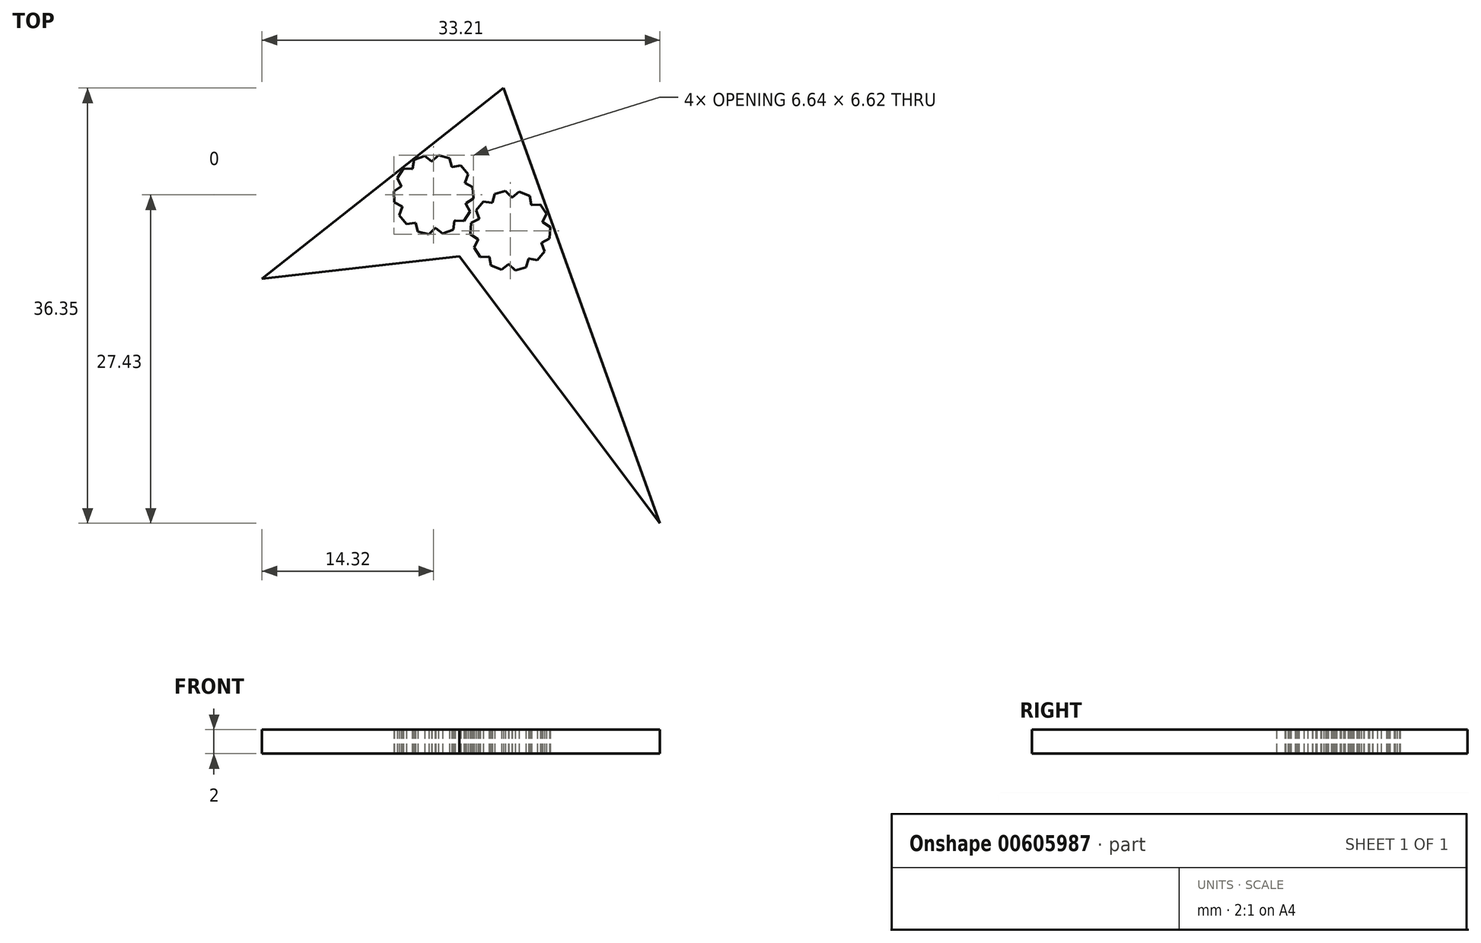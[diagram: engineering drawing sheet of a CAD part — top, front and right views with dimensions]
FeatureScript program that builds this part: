
annotation { "Feature Type Name" : "Feature", "Feature Type Description" : "" }
export const myFeature = defineFeature(function(context is Context, id is Id, definition is map)
    precondition{}
    {
        {
            var Q0;
            Q0=qCreatedBy(makeId("Top.planeOp"),FACE);
            var sketch = newSketch(context, id + "F0", { "sketchPlane" : qUnion([Q0])});
            skLineSegment(sketch, "E0", {"start": v(18, -24) * mm, "end": v(4, 15) * mm});
            skLineSegment(sketch, "E1", {"start": v(4, 15) * mm, "end": v(-17.5, -2) * mm});
            skLineSegment(sketch, "E2", {"start": v(-17.5, -2) * mm, "end": v(0, 0) * mm});
            skLineSegment(sketch, "E3", {"start": v(0, 0) * mm, "end": v(18, -24) * mm});
            skArc(sketch, "E4", {"start": v(-4.38, 6.27) * mm, "mid": v(-4.41, 6.15) * mm, "end": v(-4.45, 6.02) * mm, "construction": true});
            skLineSegment(sketch, "E5", {"start": v(-2, 8) * mm, "end": v(-1.51, 8.48) * mm});
            skLineSegment(sketch, "E6", {"start": v(-1.51, 8.48) * mm, "end": v(-0.93, 8.32) * mm});
            skLineSegment(sketch, "E7", {"start": v(-0.93, 8.32) * mm, "end": v(-0.75, 7.67) * mm});
            skLineSegment(sketch, "E8", {"start": v(-2, 5.5) * mm, "end": v(-1.22, 8.4) * mm, "construction": true});
            skLineSegment(sketch, "E9", {"start": v(-2, 8) * mm, "end": v(-2, 5.5) * mm, "construction": true});
            skLineSegment(sketch, "E10", {"start": v(-2, 5.5) * mm, "end": v(-0.75, 7.67) * mm, "construction": true});
            skLineSegment(sketch, "E11.1.0", {"start": v(-3.47, 7.52) * mm, "end": v(-3.36, 8.2) * mm});
            skLineSegment(sketch, "E11.1.1", {"start": v(-3.36, 8.2) * mm, "end": v(-2.8, 8.4) * mm});
            skLineSegment(sketch, "E11.1.2", {"start": v(-2.8, 8.4) * mm, "end": v(-2.26, 7.99) * mm});
            skLineSegment(sketch, "E11.2.0", {"start": v(-4.38, 6.27) * mm, "end": v(-4.68, 6.88) * mm});
            skLineSegment(sketch, "E11.2.1", {"start": v(-4.68, 6.88) * mm, "end": v(-4.35, 7.39) * mm});
            skLineSegment(sketch, "E11.2.2", {"start": v(-4.35, 7.39) * mm, "end": v(-3.67, 7.36) * mm});
            skLineSegment(sketch, "E11.3.0", {"start": v(-4.38, 4.73) * mm, "end": v(-4.98, 5.04) * mm});
            skLineSegment(sketch, "E11.3.1", {"start": v(-4.98, 5.04) * mm, "end": v(-5.01, 5.64) * mm});
            skLineSegment(sketch, "E11.3.2", {"start": v(-5.01, 5.64) * mm, "end": v(-4.45, 6.02) * mm});
            skLineSegment(sketch, "E11.4.0", {"start": v(-3.47, 3.48) * mm, "end": v(-4.14, 3.38) * mm});
            skLineSegment(sketch, "E11.4.1", {"start": v(-4.14, 3.38) * mm, "end": v(-4.52, 3.85) * mm});
            skLineSegment(sketch, "E11.4.2", {"start": v(-4.52, 3.85) * mm, "end": v(-4.28, 4.48) * mm});
            skLineSegment(sketch, "E11.5.0", {"start": v(-2, 3) * mm, "end": v(-2.49, 2.52) * mm});
            skLineSegment(sketch, "E11.5.1", {"start": v(-2.49, 2.52) * mm, "end": v(-3.07, 2.68) * mm});
            skLineSegment(sketch, "E11.5.2", {"start": v(-3.07, 2.68) * mm, "end": v(-3.25, 3.33) * mm});
            skLineSegment(sketch, "E11.6.0", {"start": v(-0.53, 3.48) * mm, "end": v(-0.64, 2.8) * mm});
            skLineSegment(sketch, "E11.6.1", {"start": v(-0.64, 2.8) * mm, "end": v(-1.2, 2.6) * mm});
            skLineSegment(sketch, "E11.6.2", {"start": v(-1.2, 2.6) * mm, "end": v(-1.74, 3.01) * mm});
            skLineSegment(sketch, "E11.7.0", {"start": v(0.38, 4.73) * mm, "end": v(0.68, 4.12) * mm});
            skLineSegment(sketch, "E11.7.1", {"start": v(0.68, 4.12) * mm, "end": v(0.35, 3.61) * mm});
            skLineSegment(sketch, "E11.7.2", {"start": v(0.35, 3.61) * mm, "end": v(-0.33, 3.64) * mm});
            skLineSegment(sketch, "E11.8.0", {"start": v(0.38, 6.27) * mm, "end": v(0.98, 5.96) * mm});
            skLineSegment(sketch, "E11.8.1", {"start": v(0.98, 5.96) * mm, "end": v(1.01, 5.36) * mm});
            skLineSegment(sketch, "E11.8.2", {"start": v(1.01, 5.36) * mm, "end": v(0.45, 4.98) * mm});
            skLineSegment(sketch, "E11.9.0", {"start": v(-0.53, 7.52) * mm, "end": v(0.14, 7.62) * mm});
            skLineSegment(sketch, "E11.9.1", {"start": v(0.14, 7.62) * mm, "end": v(0.52, 7.15) * mm});
            skLineSegment(sketch, "E11.9.2", {"start": v(0.52, 7.15) * mm, "end": v(0.28, 6.52) * mm});
            skArc(sketch, "E12", {"start": v(2.12, 3.52) * mm, "mid": v(2.07, 3.4) * mm, "end": v(2.02, 3.27) * mm, "construction": true});
            skLineSegment(sketch, "E13", {"start": v(3.15, 4.67) * mm, "end": v(3.33, 5.32) * mm});
            skLineSegment(sketch, "E14", {"start": v(3.33, 5.32) * mm, "end": v(3.91, 5.48) * mm});
            skLineSegment(sketch, "E15", {"start": v(3.91, 5.48) * mm, "end": v(4.4, 5) * mm});
            skLineSegment(sketch, "E16", {"start": v(4.4, 2.5) * mm, "end": v(3.62, 5.4) * mm, "construction": true});
            skLineSegment(sketch, "E17", {"start": v(3.15, 4.67) * mm, "end": v(4.4, 2.5) * mm, "construction": true});
            skLineSegment(sketch, "E18", {"start": v(4.4, 2.5) * mm, "end": v(4.4, 5) * mm, "construction": true});
            skLineSegment(sketch, "E19.1.0", {"start": v(2.12, 3.52) * mm, "end": v(1.88, 4.15) * mm});
            skLineSegment(sketch, "E19.1.1", {"start": v(1.88, 4.15) * mm, "end": v(2.26, 4.62) * mm});
            skLineSegment(sketch, "E19.1.2", {"start": v(2.26, 4.62) * mm, "end": v(2.93, 4.52) * mm});
            skLineSegment(sketch, "E19.2.0", {"start": v(1.95, 1.98) * mm, "end": v(1.39, 2.36) * mm});
            skLineSegment(sketch, "E19.2.1", {"start": v(1.39, 2.36) * mm, "end": v(1.42, 2.96) * mm});
            skLineSegment(sketch, "E19.2.2", {"start": v(1.42, 2.96) * mm, "end": v(2.02, 3.27) * mm});
            skLineSegment(sketch, "E19.3.0", {"start": v(2.73, 0.64) * mm, "end": v(2.05, 0.61) * mm});
            skLineSegment(sketch, "E19.3.1", {"start": v(2.05, 0.61) * mm, "end": v(1.72, 1.12) * mm});
            skLineSegment(sketch, "E19.3.2", {"start": v(1.72, 1.12) * mm, "end": v(2.02, 1.73) * mm});
            skLineSegment(sketch, "E19.4.0", {"start": v(4.14, 0.01) * mm, "end": v(3.6, -0.4) * mm});
            skLineSegment(sketch, "E19.4.1", {"start": v(3.6, -0.4) * mm, "end": v(3.04, -0.2) * mm});
            skLineSegment(sketch, "E19.4.2", {"start": v(3.04, -0.2) * mm, "end": v(2.93, 0.48) * mm});
            skLineSegment(sketch, "E19.5.0", {"start": v(5.65, 0.33) * mm, "end": v(5.47, -0.32) * mm});
            skLineSegment(sketch, "E19.5.1", {"start": v(5.47, -0.32) * mm, "end": v(4.89, -0.48) * mm});
            skLineSegment(sketch, "E19.5.2", {"start": v(4.89, -0.48) * mm, "end": v(4.4, 0) * mm});
            skLineSegment(sketch, "E19.6.0", {"start": v(6.68, 1.48) * mm, "end": v(6.92, 0.85) * mm});
            skLineSegment(sketch, "E19.6.1", {"start": v(6.92, 0.85) * mm, "end": v(6.54, 0.38) * mm});
            skLineSegment(sketch, "E19.6.2", {"start": v(6.54, 0.38) * mm, "end": v(5.87, 0.48) * mm});
            skLineSegment(sketch, "E19.7.0", {"start": v(6.85, 3.02) * mm, "end": v(7.41, 2.64) * mm});
            skLineSegment(sketch, "E19.7.1", {"start": v(7.41, 2.64) * mm, "end": v(7.38, 2.04) * mm});
            skLineSegment(sketch, "E19.7.2", {"start": v(7.38, 2.04) * mm, "end": v(6.78, 1.73) * mm});
            skLineSegment(sketch, "E19.8.0", {"start": v(6.07, 4.36) * mm, "end": v(6.75, 4.39) * mm});
            skLineSegment(sketch, "E19.8.1", {"start": v(6.75, 4.39) * mm, "end": v(7.08, 3.88) * mm});
            skLineSegment(sketch, "E19.8.2", {"start": v(7.08, 3.88) * mm, "end": v(6.78, 3.27) * mm});
            skLineSegment(sketch, "E19.9.0", {"start": v(4.66, 4.99) * mm, "end": v(5.2, 5.4) * mm});
            skLineSegment(sketch, "E19.9.1", {"start": v(5.2, 5.4) * mm, "end": v(5.76, 5.2) * mm});
            skLineSegment(sketch, "E19.9.2", {"start": v(5.76, 5.2) * mm, "end": v(5.87, 4.52) * mm});
            skArc(sketch, "E20", {"start": v(-4.38, 4.73) * mm, "mid": v(-4.33, 4.6) * mm, "end": v(-4.28, 4.48) * mm});
            skArc(sketch, "E21", {"start": v(2.12, 3.52) * mm, "mid": v(2.07, 3.4) * mm, "end": v(2.02, 3.27) * mm});
            skArc(sketch, "E22.trimOffspring", {"start": v(-4.38, 4.73) * mm, "mid": v(-4.33, 4.6) * mm, "end": v(-4.28, 4.48) * mm, "construction": true});
            skArc(sketch, "E23.trimOffspring", {"start": v(-3.47, 3.48) * mm, "mid": v(-3.36, 3.4) * mm, "end": v(-3.25, 3.33) * mm, "construction": true});
            skArc(sketch, "E24.trimOffspring", {"start": v(-4.38, 6.27) * mm, "mid": v(-4.41, 6.15) * mm, "end": v(-4.45, 6.02) * mm});
            skArc(sketch, "E25.trimOffspring", {"start": v(-3.47, 3.48) * mm, "mid": v(-3.36, 3.4) * mm, "end": v(-3.25, 3.33) * mm});
            skArc(sketch, "E26.trimOffspring", {"start": v(-2, 3) * mm, "mid": v(-1.87, 3) * mm, "end": v(-1.74, 3.01) * mm, "construction": true});
            skArc(sketch, "E27.trimOffspring", {"start": v(-2, 3) * mm, "mid": v(-1.87, 3) * mm, "end": v(-1.74, 3.01) * mm});
            skArc(sketch, "E28.trimOffspring", {"start": v(-0.53, 3.48) * mm, "mid": v(-0.43, 3.56) * mm, "end": v(-0.33, 3.64) * mm, "construction": true});
            skArc(sketch, "E29.trimOffspring", {"start": v(-0.53, 3.48) * mm, "mid": v(-0.43, 3.56) * mm, "end": v(-0.33, 3.64) * mm});
            skArc(sketch, "E30.trimOffspring", {"start": v(0.38, 4.73) * mm, "mid": v(0.41, 4.85) * mm, "end": v(0.45, 4.98) * mm, "construction": true});
            skArc(sketch, "E31.trimOffspring", {"start": v(0.38, 4.73) * mm, "mid": v(0.41, 4.85) * mm, "end": v(0.45, 4.98) * mm});
            skArc(sketch, "E32.trimOffspring", {"start": v(0.38, 6.27) * mm, "mid": v(0.33, 6.4) * mm, "end": v(0.28, 6.52) * mm, "construction": true});
            skArc(sketch, "E33.trimOffspring", {"start": v(0.38, 6.27) * mm, "mid": v(0.33, 6.4) * mm, "end": v(0.28, 6.52) * mm});
            skArc(sketch, "E34.trimOffspring", {"start": v(-0.53, 7.52) * mm, "mid": v(-0.64, 7.6) * mm, "end": v(-0.75, 7.67) * mm, "construction": true});
            skArc(sketch, "E35.trimOffspring", {"start": v(-0.53, 7.52) * mm, "mid": v(-0.64, 7.6) * mm, "end": v(-0.75, 7.67) * mm});
            skArc(sketch, "E36.trimOffspring", {"start": v(-3.47, 7.52) * mm, "mid": v(-3.57, 7.44) * mm, "end": v(-3.67, 7.36) * mm, "construction": true});
            skArc(sketch, "E37.trimOffspring", {"start": v(-3.47, 7.52) * mm, "mid": v(-3.57, 7.44) * mm, "end": v(-3.67, 7.36) * mm});
            skArc(sketch, "E38.trimOffspring", {"start": v(-2, 8) * mm, "mid": v(-2.13, 8) * mm, "end": v(-2.26, 7.99) * mm, "construction": true});
            skArc(sketch, "E39.trimOffspring", {"start": v(-2, 8) * mm, "mid": v(-2.13, 8) * mm, "end": v(-2.26, 7.99) * mm});
            skArc(sketch, "E40.trimOffspring", {"start": v(3.15, 4.67) * mm, "mid": v(3.04, 4.6) * mm, "end": v(2.93, 4.52) * mm, "construction": true});
            skArc(sketch, "E41.trimOffspring", {"start": v(3.15, 4.67) * mm, "mid": v(3.04, 4.6) * mm, "end": v(2.93, 4.52) * mm});
            skArc(sketch, "E42.trimOffspring", {"start": v(4.66, 4.99) * mm, "mid": v(4.53, 5) * mm, "end": v(4.4, 5) * mm, "construction": true});
            skArc(sketch, "E43.trimOffspring", {"start": v(4.66, 4.99) * mm, "mid": v(4.53, 5) * mm, "end": v(4.4, 5) * mm});
            skArc(sketch, "E44.trimOffspring", {"start": v(6.07, 4.36) * mm, "mid": v(5.97, 4.44) * mm, "end": v(5.87, 4.52) * mm, "construction": true});
            skArc(sketch, "E45.trimOffspring", {"start": v(6.07, 4.36) * mm, "mid": v(5.97, 4.44) * mm, "end": v(5.87, 4.52) * mm});
            skArc(sketch, "E46.trimOffspring", {"start": v(6.85, 3.02) * mm, "mid": v(6.81, 3.15) * mm, "end": v(6.78, 3.27) * mm, "construction": true});
            skArc(sketch, "E47.trimOffspring", {"start": v(6.85, 3.02) * mm, "mid": v(6.81, 3.15) * mm, "end": v(6.78, 3.27) * mm});
            skArc(sketch, "E48.trimOffspring", {"start": v(6.68, 1.48) * mm, "mid": v(6.73, 1.6) * mm, "end": v(6.78, 1.73) * mm, "construction": true});
            skArc(sketch, "E49.trimOffspring", {"start": v(6.68, 1.48) * mm, "mid": v(6.73, 1.6) * mm, "end": v(6.78, 1.73) * mm});
            skArc(sketch, "E50.trimOffspring", {"start": v(5.65, 0.33) * mm, "mid": v(5.76, 0.4) * mm, "end": v(5.87, 0.48) * mm, "construction": true});
            skArc(sketch, "E51.trimOffspring", {"start": v(5.65, 0.33) * mm, "mid": v(5.76, 0.4) * mm, "end": v(5.87, 0.48) * mm});
            skArc(sketch, "E52.trimOffspring", {"start": v(4.14, 0.01) * mm, "mid": v(4.27, 0) * mm, "end": v(4.4, 0) * mm, "construction": true});
            skArc(sketch, "E53.trimOffspring", {"start": v(4.14, 0.01) * mm, "mid": v(4.27, 0) * mm, "end": v(4.4, 0) * mm});
            skArc(sketch, "E54.trimOffspring", {"start": v(2.73, 0.64) * mm, "mid": v(2.83, 0.56) * mm, "end": v(2.93, 0.48) * mm, "construction": true});
            skArc(sketch, "E55.trimOffspring", {"start": v(2.73, 0.64) * mm, "mid": v(2.83, 0.56) * mm, "end": v(2.93, 0.48) * mm});
            skArc(sketch, "E56.trimOffspring", {"start": v(1.95, 1.98) * mm, "mid": v(1.99, 1.85) * mm, "end": v(2.02, 1.73) * mm, "construction": true});
            skArc(sketch, "E57.trimOffspring", {"start": v(1.95, 1.98) * mm, "mid": v(1.99, 1.85) * mm, "end": v(2.02, 1.73) * mm});
            skLineSegment(sketch, "E58.0", {"start": v(-4.62, 4.52) * mm, "end": v(-5.27, 4.86) * mm});
            skArc(sketch, "E58.1", {"start": v(-4.62, 4.52) * mm, "mid": v(-4.61, 4.5) * mm, "end": v(-4.6, 4.48) * mm});
            skLineSegment(sketch, "E58.2", {"start": v(-4.86, 3.79) * mm, "end": v(-4.6, 4.48) * mm});
            skLineSegment(sketch, "E58.3", {"start": v(-4.27, 3.06) * mm, "end": v(-4.86, 3.79) * mm});
            skLineSegment(sketch, "E58.4", {"start": v(-3.54, 3.16) * mm, "end": v(-4.27, 3.06) * mm});
            skArc(sketch, "E58.5", {"start": v(-3.54, 3.16) * mm, "mid": v(-3.52, 3.15) * mm, "end": v(-3.5, 3.14) * mm});
            skLineSegment(sketch, "E58.6", {"start": v(-3.3, 2.43) * mm, "end": v(-3.5, 3.14) * mm});
            skLineSegment(sketch, "E58.7", {"start": v(-2.4, 2.2) * mm, "end": v(-3.3, 2.43) * mm});
            skLineSegment(sketch, "E58.8", {"start": v(-1.87, 2.7) * mm, "end": v(-2.4, 2.2) * mm});
            skArc(sketch, "E58.9", {"start": v(-1.87, 2.7) * mm, "mid": v(-1.85, 2.7) * mm, "end": v(-1.83, 2.7) * mm});
            skLineSegment(sketch, "E58.10", {"start": v(-1.26, 2.25) * mm, "end": v(-1.83, 2.7) * mm});
            skLineSegment(sketch, "E58.11", {"start": v(-5.27, 4.86) * mm, "end": v(-5.32, 5.8) * mm});
            skLineSegment(sketch, "E58.12", {"start": v(-0.38, 2.59) * mm, "end": v(-1.26, 2.25) * mm});
            skLineSegment(sketch, "E58.13", {"start": v(-0.25, 3.31) * mm, "end": v(-0.38, 2.59) * mm});
            skArc(sketch, "E58.14", {"start": v(-0.25, 3.31) * mm, "mid": v(-0.24, 3.32) * mm, "end": v(-0.22, 3.34) * mm});
            skLineSegment(sketch, "E58.15", {"start": v(0.51, 3.3) * mm, "end": v(-0.22, 3.34) * mm});
            skLineSegment(sketch, "E58.16", {"start": v(1.02, 4.1) * mm, "end": v(0.51, 3.3) * mm});
            skLineSegment(sketch, "E58.17", {"start": v(0.7, 4.75) * mm, "end": v(1.02, 4.1) * mm});
            skArc(sketch, "E58.18", {"start": v(-2.13, 8.3) * mm, "mid": v(-2.15, 8.3) * mm, "end": v(-2.17, 8.3) * mm});
            skLineSegment(sketch, "E58.19", {"start": v(-2.74, 8.75) * mm, "end": v(-2.17, 8.3) * mm});
            skLineSegment(sketch, "E58.20", {"start": v(-3.62, 8.41) * mm, "end": v(-2.74, 8.75) * mm});
            skLineSegment(sketch, "E58.21", {"start": v(-3.75, 7.69) * mm, "end": v(-3.62, 8.41) * mm});
            skArc(sketch, "E58.22", {"start": v(-3.75, 7.69) * mm, "mid": v(-3.76, 7.68) * mm, "end": v(-3.78, 7.66) * mm});
            skLineSegment(sketch, "E58.23", {"start": v(-4.51, 7.7) * mm, "end": v(-3.78, 7.66) * mm});
            skLineSegment(sketch, "E58.24", {"start": v(-5.32, 5.8) * mm, "end": v(-4.71, 6.2) * mm});
            skArc(sketch, "E58.25", {"start": v(-4.7, 6.25) * mm, "mid": v(-4.7, 6.22) * mm, "end": v(-4.71, 6.2) * mm});
            skLineSegment(sketch, "E58.26", {"start": v(-4.7, 6.25) * mm, "end": v(-5.02, 6.9) * mm});
            skLineSegment(sketch, "E58.27", {"start": v(-5.02, 6.9) * mm, "end": v(-4.51, 7.7) * mm});
            skLineSegment(sketch, "E58.28", {"start": v(-2.13, 8.3) * mm, "end": v(-1.6, 8.8) * mm});
            skLineSegment(sketch, "E58.29", {"start": v(-1.6, 8.8) * mm, "end": v(-0.7, 8.57) * mm});
            skLineSegment(sketch, "E58.30", {"start": v(-0.7, 8.57) * mm, "end": v(-0.5, 7.86) * mm});
            skArc(sketch, "E58.31", {"start": v(-0.46, 7.84) * mm, "mid": v(-0.48, 7.85) * mm, "end": v(-0.5, 7.86) * mm});
            skLineSegment(sketch, "E58.32", {"start": v(-0.46, 7.84) * mm, "end": v(0.27, 7.94) * mm});
            skLineSegment(sketch, "E58.33", {"start": v(0.27, 7.94) * mm, "end": v(0.86, 7.21) * mm});
            skLineSegment(sketch, "E58.34", {"start": v(0.86, 7.21) * mm, "end": v(0.6, 6.52) * mm});
            skArc(sketch, "E58.35", {"start": v(0.62, 6.48) * mm, "mid": v(0.61, 6.5) * mm, "end": v(0.6, 6.52) * mm});
            skLineSegment(sketch, "E58.36", {"start": v(0.62, 6.48) * mm, "end": v(1.27, 6.14) * mm});
            skLineSegment(sketch, "E58.37", {"start": v(1.27, 6.14) * mm, "end": v(1.32, 5.2) * mm});
            skLineSegment(sketch, "E58.38", {"start": v(1.32, 5.2) * mm, "end": v(0.71, 4.8) * mm});
            skArc(sketch, "E58.39", {"start": v(0.7, 4.75) * mm, "mid": v(0.7, 4.78) * mm, "end": v(0.71, 4.8) * mm});
            skLineSegment(sketch, "E59.0", {"start": v(2.9, 4.86) * mm, "end": v(3.1, 5.57) * mm});
            skArc(sketch, "E59.1", {"start": v(2.9, 4.86) * mm, "mid": v(2.88, 4.85) * mm, "end": v(2.86, 4.84) * mm});
            skLineSegment(sketch, "E59.2", {"start": v(2.13, 4.94) * mm, "end": v(2.86, 4.84) * mm});
            skLineSegment(sketch, "E59.3", {"start": v(1.54, 4.21) * mm, "end": v(2.13, 4.94) * mm});
            skLineSegment(sketch, "E59.4", {"start": v(1.8, 3.52) * mm, "end": v(1.54, 4.21) * mm});
            skArc(sketch, "E59.5", {"start": v(1.8, 3.52) * mm, "mid": v(1.79, 3.5) * mm, "end": v(1.78, 3.48) * mm});
            skLineSegment(sketch, "E59.6", {"start": v(1.13, 3.14) * mm, "end": v(1.78, 3.48) * mm});
            skLineSegment(sketch, "E59.7", {"start": v(1.08, 2.2) * mm, "end": v(1.13, 3.14) * mm});
            skLineSegment(sketch, "E59.8", {"start": v(1.69, 1.8) * mm, "end": v(1.08, 2.2) * mm});
            skArc(sketch, "E59.9", {"start": v(1.69, 1.8) * mm, "mid": v(1.7, 1.78) * mm, "end": v(1.7, 1.75) * mm});
            skLineSegment(sketch, "E59.10", {"start": v(1.38, 1.1) * mm, "end": v(1.7, 1.75) * mm});
            skLineSegment(sketch, "E59.11", {"start": v(3.1, 5.57) * mm, "end": v(4, 5.8) * mm});
            skLineSegment(sketch, "E59.12", {"start": v(1.89, 0.3) * mm, "end": v(1.38, 1.1) * mm});
            skLineSegment(sketch, "E59.13", {"start": v(2.62, 0.34) * mm, "end": v(1.89, 0.3) * mm});
            skArc(sketch, "E59.14", {"start": v(2.62, 0.34) * mm, "mid": v(2.64, 0.32) * mm, "end": v(2.65, 0.31) * mm});
            skLineSegment(sketch, "E59.15", {"start": v(2.78, -0.41) * mm, "end": v(2.65, 0.31) * mm});
            skLineSegment(sketch, "E59.16", {"start": v(3.66, -0.75) * mm, "end": v(2.78, -0.41) * mm});
            skLineSegment(sketch, "E59.17", {"start": v(4.23, -0.3) * mm, "end": v(3.66, -0.75) * mm});
            skArc(sketch, "E59.18", {"start": v(7.11, 3.2) * mm, "mid": v(7.1, 3.22) * mm, "end": v(7.1, 3.25) * mm});
            skLineSegment(sketch, "E59.19", {"start": v(7.42, 3.9) * mm, "end": v(7.1, 3.25) * mm});
            skLineSegment(sketch, "E59.20", {"start": v(6.91, 4.7) * mm, "end": v(7.42, 3.9) * mm});
            skLineSegment(sketch, "E59.21", {"start": v(6.18, 4.66) * mm, "end": v(6.91, 4.7) * mm});
            skArc(sketch, "E59.22", {"start": v(6.18, 4.66) * mm, "mid": v(6.16, 4.68) * mm, "end": v(6.15, 4.69) * mm});
            skLineSegment(sketch, "E59.23", {"start": v(6.02, 5.41) * mm, "end": v(6.15, 4.69) * mm});
            skLineSegment(sketch, "E59.24", {"start": v(4, 5.8) * mm, "end": v(4.53, 5.3) * mm});
            skArc(sketch, "E59.25", {"start": v(4.57, 5.3) * mm, "mid": v(4.55, 5.3) * mm, "end": v(4.53, 5.3) * mm});
            skLineSegment(sketch, "E59.26", {"start": v(4.57, 5.3) * mm, "end": v(5.14, 5.75) * mm});
            skLineSegment(sketch, "E59.27", {"start": v(5.14, 5.75) * mm, "end": v(6.02, 5.41) * mm});
            skLineSegment(sketch, "E59.28", {"start": v(7.11, 3.2) * mm, "end": v(7.72, 2.8) * mm});
            skLineSegment(sketch, "E59.29", {"start": v(7.72, 2.8) * mm, "end": v(7.67, 1.86) * mm});
            skLineSegment(sketch, "E59.30", {"start": v(7.67, 1.86) * mm, "end": v(7.02, 1.52) * mm});
            skArc(sketch, "E59.31", {"start": v(7, 1.48) * mm, "mid": v(7.01, 1.5) * mm, "end": v(7.02, 1.52) * mm});
            skLineSegment(sketch, "E59.32", {"start": v(7, 1.48) * mm, "end": v(7.26, 0.79) * mm});
            skLineSegment(sketch, "E59.33", {"start": v(7.26, 0.79) * mm, "end": v(6.67, 0.06) * mm});
            skLineSegment(sketch, "E59.34", {"start": v(6.67, 0.06) * mm, "end": v(5.94, 0.16) * mm});
            skArc(sketch, "E59.35", {"start": v(5.9, 0.14) * mm, "mid": v(5.92, 0.15) * mm, "end": v(5.94, 0.16) * mm});
            skLineSegment(sketch, "E59.36", {"start": v(5.9, 0.14) * mm, "end": v(5.7, -0.57) * mm});
            skLineSegment(sketch, "E59.37", {"start": v(5.7, -0.57) * mm, "end": v(4.8, -0.8) * mm});
            skLineSegment(sketch, "E59.38", {"start": v(4.8, -0.8) * mm, "end": v(4.27, -0.3) * mm});
            skArc(sketch, "E59.39", {"start": v(4.23, -0.3) * mm, "mid": v(4.25, -0.3) * mm, "end": v(4.27, -0.3) * mm});
            skLineSegment(sketch, "E60.0", {"start": v(3.84, 14.42) * mm, "end": v(-16.32, -1.51) * mm});
            skLineSegment(sketch, "E60.1", {"start": v(16.89, -21.93) * mm, "end": v(3.84, 14.42) * mm});
            skLineSegment(sketch, "E60.2", {"start": v(0.16, 0.37) * mm, "end": v(16.89, -21.93) * mm});
            skLineSegment(sketch, "E60.3", {"start": v(-16.32, -1.51) * mm, "end": v(0.16, 0.37) * mm});
            skSolve(sketch);
        }
        {
            var Q0;
            Q0=makeQuery(id+"F0.imprint","IMPRINT",FACE,{"disambiguationData":[TD([[makeQuery(id+"F0.imprint","IMPRINT",EDGE,{"derivedFrom":sQuery(id+"F0.wireOp",EDGE,"E58.0")}),1.0]])]});
            extrude(context, id + "F1", {"entities" : qUnion([Q0]), "depth" : 2 * mm});
        }
    });
